# Revit family: 1699-W
name_source: partatom
category: Plumbing Fixtures
revit_build: Autodesk Revit MEP 2016 (Build: 20150220_1215(x64)
units: mm (PartAtom-declared; Revit-internal decimal feet)

## family parameters
Cut with Voids When Loaded = Yes
Host = Face
OmniClass Number = 23.45.05.14.31.14
OmniClass Title = Detention Combination Toilets
Part Type = Normal
Room Calculation Point = No
Round Connector Dimension = Use Diameter
Shared = Yes

## types (1)
- 1699-W
    1.6 GPF (Not Available in California) = No
    1699 Detox Toilet with Flange = Yes
    3.5 GPF (Not Available in California) = No
    Assembly Code = D2030400
    CW Connection = No
    CWFU = 3
    Cold Water Connection Diameter = 1"
    Connection Size = 2 3/8"
    DLF - Detox Less Flange = No
    Default Elevation = 0"
    Description = Penal-Ware 1699 Series Detox Toilet - Blowout Jet Type - Remote Flushing
    Drain Extension = 10"
    EVSFV Master-Trol® Electronic Flush Valve = No
    EVSPFV Master-Trol® Electronic Flush Valve w/ Piezo Button = No
    FV - Flush Valve, Mechanical = No
    FVBO - Flush Valve by Others = No
    FVH - Flush Valve, Hydraulic = No
    FVL Flush Valve, Lever Handle (Wall Supply) = No
    Grid Length Opening = 12"
    Grid width opening = 8"
    HW Connection = No
    HWFU = 3
    Height = 12 1/2"
    Inlet Depth = 1 7/8"
    Inlet Extention N-C = 5"
    Installation Instruction Link = https://www.acorneng.com
    Length = 14"
    MTPFV Master-Trol PLUS Electronic Flush Valve = No
    MTPPFV Master-Trol PLUS Electronic Flush Valve w/ Piezo = No
    MVCFV - Time-Trol Electronic Flush Valve = No
    Manufacturer = Acorn
    Material = Metal-Acorn-Stainless Steel_Brushed
    Model = 1699-W
    Product Documentation Link = https://www.acorneng.com
    Product Page URL = https://www.acorneng.com
    TF Transformer, 120VAC to 24VAC (-MVCFV option) = No
    URL = http://www.acorneng.com
    VAC - AcornVac System = No
    Vent Connection = No
    W - Wall (Concealed) = Yes
    WFU = 4
    Warranty Documentation Link = www.acorneng.com/terms-and-conditions
    Waste Connection = Yes
    Waste Outlet Depth = 4 1/4"
    Width = 10"

## geometry (parser evidence)
native form markers: Sweep x1
no freeform markers — native parametric forms only
